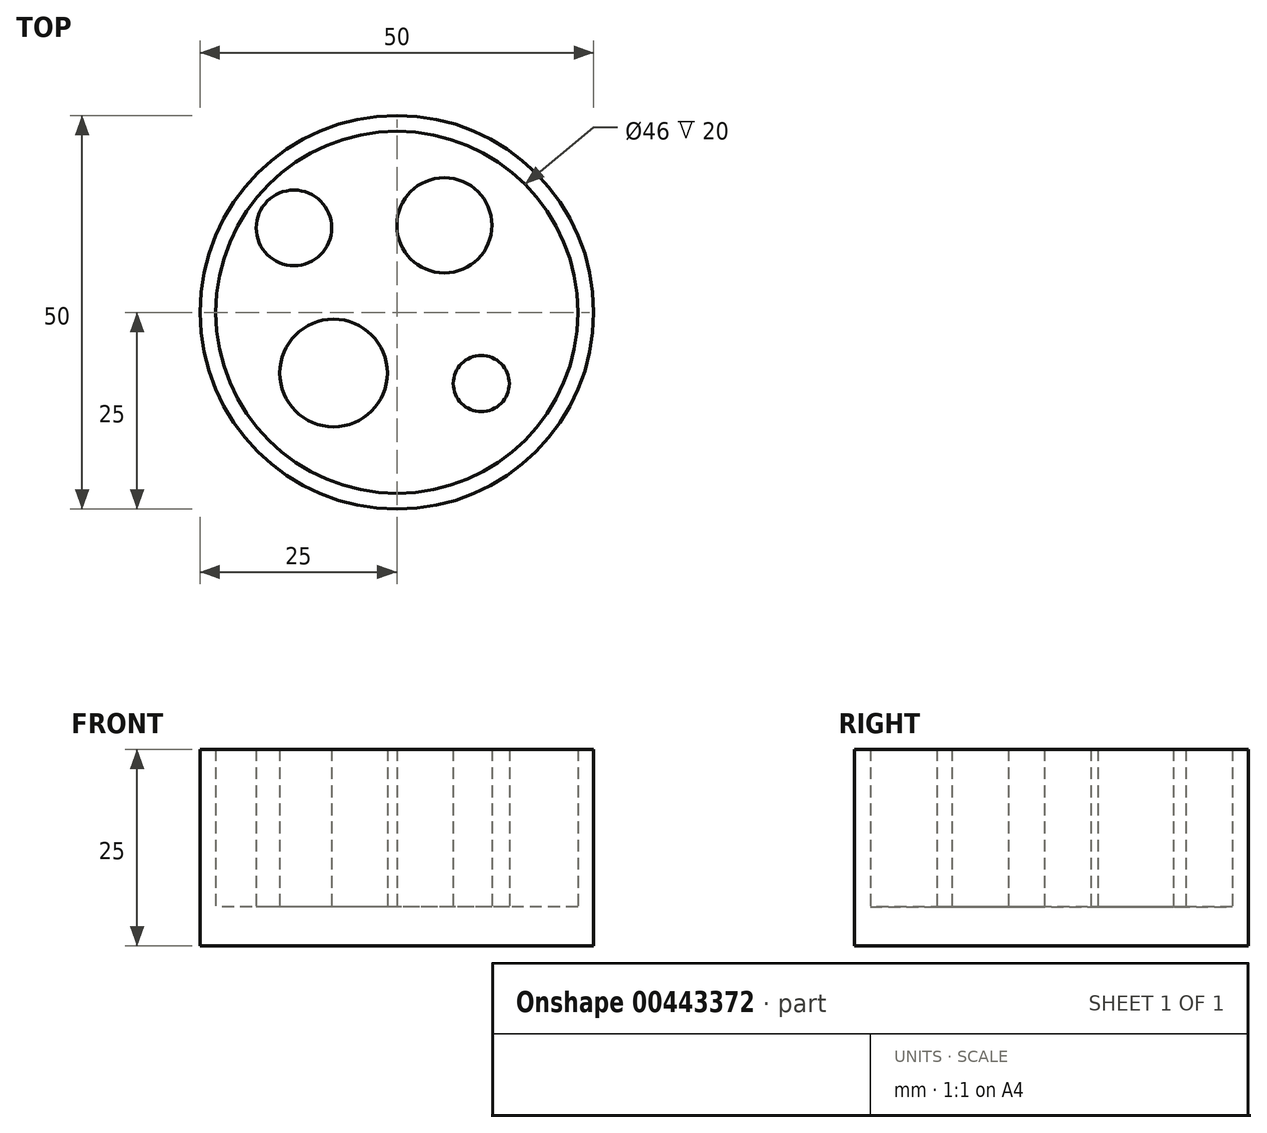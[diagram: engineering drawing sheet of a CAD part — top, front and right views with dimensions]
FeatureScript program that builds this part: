
annotation { "Feature Type Name" : "Feature", "Feature Type Description" : "" }
export const myFeature = defineFeature(function(context is Context, id is Id, definition is map)
    precondition{}
    {
        {
            var Q0;
            Q0=qCreatedBy(makeId("Top.planeOp"),FACE);
            var sketch = newSketch(context, id + "F0", { "sketchPlane" : qUnion([Q0])});
            skCircle(sketch, "E0", {"center": v(0, 0) * mm, "radius": 25 * mm});
            skCircle(sketch, "E1", {"center": v(0, 0) * mm, "radius": 23 * mm});
            skCircle(sketch, "E2", {"center": v(-13.07, 10.72) * mm, "radius": 4.8 * mm});
            skCircle(sketch, "E3", {"center": v(-8.04, -7.7) * mm, "radius": 6.83 * mm});
            skCircle(sketch, "E4", {"center": v(10.72, -9.05) * mm, "radius": 3.56 * mm});
            skCircle(sketch, "E5", {"center": v(6.03, 11.06) * mm, "radius": 6.04 * mm});
            skSolve(sketch);
        }
        {
            var Q0;
            Q0 = qSketchRegion(id + "F0", true);
            extrude(context, id + "F1", {"entities" : qUnion([Q0]), "depth" : 25 * mm});
        }
        {
            var Q0;
            Q0=makeQuery(id+"F0.imprint","IMPRINT",FACE,{"disambiguationData":[TD([[makeQuery(id+"F0.imprint","IMPRINT",EDGE,{"derivedFrom":sQuery(id+"F0.wireOp",EDGE,"E1")}),1.0]])]});
            extrude(context, id + "F2", {"entities" : qUnion([Q0]), "operationType" : NewBodyOperationType.ADD, "depth" : 5 * mm});
        }
        {
            var Q0;
            Q0=makeQuery(id+"F0.imprint","IMPRINT",FACE,{"disambiguationData":[TD([[makeQuery(id+"F0.imprint","IMPRINT",EDGE,{"derivedFrom":sQuery(id+"F0.wireOp",EDGE,"E3")}),1.0]])]});
            var Q1;
            Q1=makeQuery(id+"F0.imprint","IMPRINT",FACE,{"disambiguationData":[TD([[makeQuery(id+"F0.imprint","IMPRINT",EDGE,{"derivedFrom":sQuery(id+"F0.wireOp",EDGE,"E5")}),1.0]])]});
            var Q2;
            Q2=makeQuery(id+"F0.imprint","IMPRINT",FACE,{"disambiguationData":[TD([[makeQuery(id+"F0.imprint","IMPRINT",EDGE,{"derivedFrom":sQuery(id+"F0.wireOp",EDGE,"E2")}),1.0]])]});
            var Q3;
            Q3=makeQuery(id+"F0.imprint","IMPRINT",FACE,{"disambiguationData":[TD([[makeQuery(id+"F0.imprint","IMPRINT",EDGE,{"derivedFrom":sQuery(id+"F0.wireOp",EDGE,"E4")}),1.0]])]});
            extrude(context, id + "F3", {"entities" : qUnion([Q0, Q1, Q2, Q3]), "operationType" : NewBodyOperationType.ADD, "depth" : 25 * mm});
        }
    });
